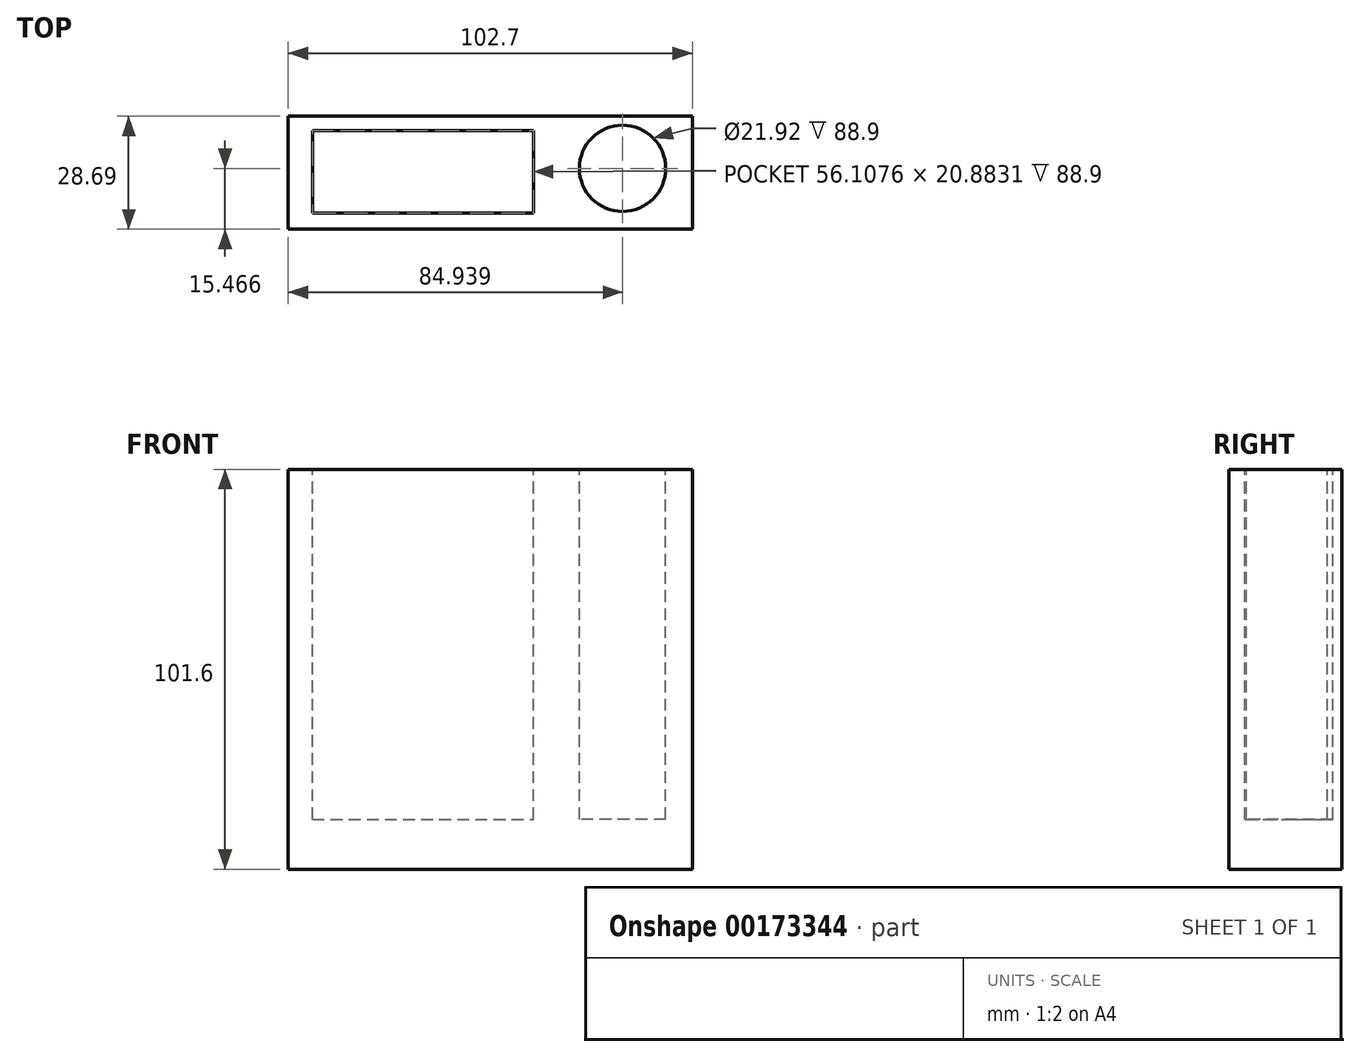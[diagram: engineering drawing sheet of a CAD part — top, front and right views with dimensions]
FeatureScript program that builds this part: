
annotation { "Feature Type Name" : "Feature", "Feature Type Description" : "" }
export const myFeature = defineFeature(function(context is Context, id is Id, definition is map)
    precondition{}
    {
        {
            var Q0;
            Q0=qCreatedBy(makeId("Top.planeOp"),FACE);
            var sketch = newSketch(context, id + "F0", { "sketchPlane" : qUnion([Q0])});
            skLineSegment(sketch, "E0.bottom", {"start": v(-55.25, -22) * mm, "end": v(47.45, -22) * mm});
            skLineSegment(sketch, "E0.top", {"start": v(-55.25, 6.68) * mm, "end": v(47.45, 6.68) * mm});
            skLineSegment(sketch, "E0.left", {"start": v(-55.25, -22) * mm, "end": v(-55.25, 6.68) * mm});
            skLineSegment(sketch, "E0.right", {"start": v(47.45, -22) * mm, "end": v(47.45, 6.68) * mm});
            skSolve(sketch);
        }
        {
            var Q0;
            Q0 = qSketchRegion(id + "F0", true);
            extrude(context, id + "F1", {"entities" : qUnion([Q0]), "depth" : 101.6 * mm});
        }
        {
            var Q0;
            Q0=makeQuery(id+"F1.opExtrude","CAP_FACE",FACE,{"disambiguationData":[OSD([sQuery(id+"F0.wireOp",EDGE,"E0.bottom"),sQuery(id+"F0.wireOp",EDGE,"E0.top"),sQuery(id+"F0.wireOp",EDGE,"E0.left"),sQuery(id+"F0.wireOp",EDGE,"E0.right")])],"isStart":false});
            var sketch = newSketch(context, id + "F2", { "sketchPlane" : qUnion([Q0])});
            skLineSegment(sketch, "E1.top", {"start": v(-49.06, -17.87) * mm, "end": v(7.04, -17.87) * mm});
            skLineSegment(sketch, "E1.left", {"start": v(-49.06, 0) * mm, "end": v(-49.06, -17.87) * mm});
            skLineSegment(sketch, "E1.right", {"start": v(7.04, 0) * mm, "end": v(7.04, -17.87) * mm});
            skLineSegment(sketch, "E2.top", {"start": v(-49.06, 3.02) * mm, "end": v(7.04, 3.02) * mm});
            skLineSegment(sketch, "E2.left", {"start": v(-49.06, 0) * mm, "end": v(-49.06, 3.02) * mm});
            skLineSegment(sketch, "E2.right", {"start": v(7.04, 0) * mm, "end": v(7.04, 3.02) * mm});
            skSolve(sketch);
        }
        {
            var Q0;
            Q0 = qSketchRegion(id + "F2", true);
            extrude(context, id + "F3", {"entities" : qUnion([Q0]), "operationType" : NewBodyOperationType.REMOVE, "oppositeDirection" : true, "depth" : 88.9 * mm});
        }
        {
            var Q0;
            Q0=makeQuery(id+"F1.opExtrude","CAP_FACE",FACE,{"disambiguationData":[OSD([sQuery(id+"F0.wireOp",EDGE,"E0.bottom"),sQuery(id+"F0.wireOp",EDGE,"E0.top"),sQuery(id+"F0.wireOp",EDGE,"E0.left"),sQuery(id+"F0.wireOp",EDGE,"E0.right")])],"isStart":false});
            var sketch = newSketch(context, id + "F4", { "sketchPlane" : qUnion([Q0])});
            skCircle(sketch, "E3", {"center": v(29.69, -6.54) * mm, "radius": 10.96 * mm});
            skSolve(sketch);
        }
        {
            var Q0;
            Q0 = qSketchRegion(id + "F4", true);
            var Q1;
            Q1=makeQuery(id+"F4.imprint","IMPRINT",FACE,{"disambiguationData":[TD([[makeQuery(id+"F4.imprint","IMPRINT",EDGE,{"derivedFrom":makeQuery(id+"F3.boolean.opBoolean","COPY",EDGE,{"derivedFrom":makeQuery(id+"F3.opExtrude","CAP_EDGE",EDGE,{"disambiguationData":[OSD([sQuery(id+"F2.wireOp",EDGE,"E1.top")])],"isStart":true})})}),1.0]])]});
            extrude(context, id + "F5", {"entities" : qUnion([Q0, Q1]), "operationType" : NewBodyOperationType.REMOVE, "oppositeDirection" : true, "depth" : 88.9 * mm});
        }
    });
